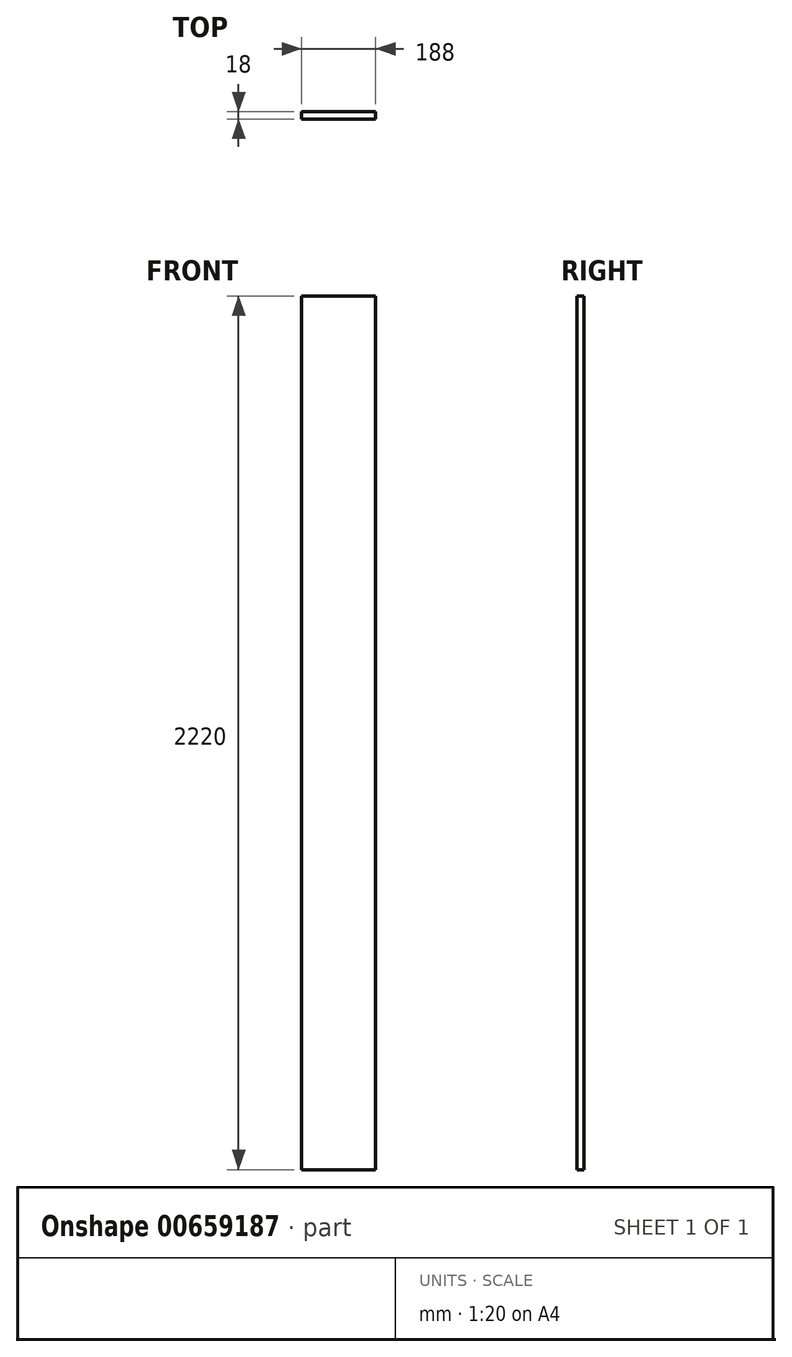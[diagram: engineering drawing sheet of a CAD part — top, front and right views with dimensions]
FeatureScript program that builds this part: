
annotation { "Feature Type Name" : "Feature", "Feature Type Description" : "" }
export const myFeature = defineFeature(function(context is Context, id is Id, definition is map)
    precondition{}
    {
        {
            var Q0;
            Q0=qCreatedBy(makeId("Front.planeOp"),FACE);
            var sketch = newSketch(context, id + "F0", { "sketchPlane" : qUnion([Q0])});
            skLineSegment(sketch, "E0.bottom", {"start": v(-94, -1110) * mm, "end": v(94, -1110) * mm});
            skLineSegment(sketch, "E0.top", {"start": v(-94, 1110) * mm, "end": v(94, 1110) * mm});
            skLineSegment(sketch, "E0.left", {"start": v(-94, -1110) * mm, "end": v(-94, 1110) * mm});
            skLineSegment(sketch, "E0.right", {"start": v(94, -1110) * mm, "end": v(94, 1110) * mm});
            skPoint(sketch, "E0.middle", {"position": v(0, 0) * mm});
            skSolve(sketch);
        }
        {
            var Q0;
            Q0=makeQuery(id+"F0.imprint","IMPRINT",FACE,{"disambiguationData":[TD([[makeQuery(id+"F0.imprint","IMPRINT",EDGE,{"derivedFrom":sQuery(id+"F0.wireOp",EDGE,"E0.bottom")}),1.0]])]});
            extrude(context, id + "F1", {"entities" : qUnion([Q0]), "endBound" : BoundingType.SYMMETRIC, "depth" : 18 * mm, "offsetDistance" : 25 * mm});
        }
    });
